# Revit family: Hager-UNIVERS-Hollow_wall-IP30-With_Cover-With_DIN-NoHosted-AT-de
name_source: partatom
category: Electrical Equipment
units: mm (PartAtom-declared; Revit-internal decimal feet)

## family parameters
Always vertical = Yes
Cut with Voids When Loaded = No
Maintain Annotation Orientation = No
Panel Configuration = Two Columns, Circuits Across
Part Type = Panelboard
Room Calculation Point = No
Round Connector Dimension = Use Diameter
Shared = No
Work Plane-Based = Yes

## types (21) — shared parameters
Code hager = ADD-EC000214_EU
Default Elevation = 1200 mm
EF000003 - Montageart = Hohlwand
EF000007 - Farbe = weiß
EF000024 - UV-beständig = No
EF000049 - Tiefe = 125 mm  [stored 0.410105 ft]
EF000116 - RAL-Nummer = 9010
EF000218 - Einbautiefe = 112 mm  [stored 0.367454 ft]
EF001062 - EMV-Ausführung = No
EF001088 - Anbaumöglichkeit = Yes
EF001134 - DIN-Schiene = Yes
EF004462 - Art der Schließung = sonstige
EF005474 - Schutzart (IP) = IP30
EF006244 - Transparenter Deckel/Tür = No
EF006306 - Mit Schloss = No
EF009212 - Ausführung Deckel = mit Ausschnitt
EF015776 - Erdungsklemmenblock = Yes
ETIM class code = EC000214
ETIM class name = Small distribution board
HG000002-Mit tür = Yes
HG000003-Bereich = UNIVERS
HG000005-Dicke = 2 mm  [stored 0.00656168 ft]
HG000006-Flush mounted = Yes
HG000012-Türschwenkwinkel = 90.00°
HG000013-Tür links = No
HG000014-Tür rechts = Yes
HG000015-Sichtbarkeit der Türöffnung = Yes
HG000016-3D-Türsichtbarkeit = Yes
HG000017-Distanz zwischen den Polen = 18 mm  [stored 0.0590551 ft]
HG000060-RAL-number = 9010
HG000099-Onfly Template ID-de-DE = 507532
Manufacturer = Hager
Name BIM&CO = Electricity
Name hager = ADD_Enclosures_EC000214
Reference = Template-Enclosure_EU-EC000214
Uniformat = Low Tension Service & Dist.
Uniformat code = D501001
zero-valued in all types: EF001131 - Innentiefe, HG000007-Anzahl der leeren Spalten

## per-type parameters (varying)
| type | BC_METADATA | EF000008 - Breite | EF000040 - Höhe | EF000118 - Mit Montageplatte | EF000266 - Anzahl der Reihen | EF000332 - Einbauhöhe | EF000846 - Einbaubreite | EF002950 - Breite in Teilungseinheiten | EF015777 - Neutralleiterklemmenblock | EF015941 - Signaldurchlassende Tür | HG000001-Anzahl der Spalten | HG000004-Herstellerreferenz | HG000008-Anzahl der leeren Reihen | HG000009-Doppelflügeligen Tür | HG000010-Asymmetrische Türen | HG000011-Leere Reihen von unten | HGEF000266-Anzahl der Reihen | HGEF0002950-Breite in Teilungseinheiten |
| UNIVERS-Hollow_wall_W603_H1153_D125_26_Modular_Spacing-FWU72M5 | {"ObjectGuid":"bf8f3bd7-583b-483a-8546-479ce88145ff","ModelGuid":"46e0040d-b32f-415f-bc34-bf38312fe43a","VariantGuid":"83216833-e940-4f8e-bb07-8edc410ff69f","Revision":"#6","VariantName":"UNIVERS-Hollow_wall_W603_H1153_D125_26_Modular_Spacing-FWU72M5"} | 603 mm | 1153 mm | No | 7 | 1102 mm  [stored 3.61549 ft] | 560 mm  [stored 1.83727 ft] | 26 | No | Yes | 1 | FWU72M5 | 4 | No | No | Yes | 7 | 26 |
| UNIVERS-Hollow_wall_W603_H1153_D125_24_Modular_Spacing-FWU72N2 | {"ObjectGuid":"bf8f3bd7-583b-483a-8546-479ce88145ff","ModelGuid":"46e0040d-b32f-415f-bc34-bf38312fe43a","VariantGuid":"d2052f01-a17f-49fd-b384-75a0194649ad","Revision":"#6","VariantName":"UNIVERS-Hollow_wall_W603_H1153_D125_24_Modular_Spacing-FWU72N2"} | 603 mm | 1153 mm | No | 7 | 1102 mm  [stored 3.61549 ft] | 560 mm  [stored 1.83727 ft] | 24 | No | No | 1 | FWU72N2 | 2 | No | No | No | 7 | 24 |
| UNIVERS-Hollow_wall_W603_H1153_D125_12_Modular_Spacing-FWU72S | {"ObjectGuid":"bf8f3bd7-583b-483a-8546-479ce88145ff","ModelGuid":"46e0040d-b32f-415f-bc34-bf38312fe43a","VariantGuid":"2965ec61-e6e9-4a88-9c4b-0654146b79c7","Revision":"#6","VariantName":"UNIVERS-Hollow_wall_W603_H1153_D125_12_Modular_Spacing-FWU72S"} | 603 mm | 1153 mm | No | 7 | 1102 mm  [stored 3.61549 ft] | 560 mm  [stored 1.83727 ft] | 12 | No | No | 2 | FWU72S | 0 | No | No | No | 7 | 12 |
| UNIVERS-Hollow_wall_W853_H1153_D125_12_Modular_Spacing-FWU73S | {"ObjectGuid":"bf8f3bd7-583b-483a-8546-479ce88145ff","ModelGuid":"46e0040d-b32f-415f-bc34-bf38312fe43a","VariantGuid":"00a44853-eb4c-43b7-9f09-506ca887cdd2","Revision":"#6","VariantName":"UNIVERS-Hollow_wall_W853_H1153_D125_12_Modular_Spacing-FWU73S"} | 853 mm  [stored 2.79856 ft] | 1153 mm | No | 7 | 1102 mm  [stored 3.61549 ft] | 810 mm | 12 | Yes | No | 3 | FWU73S | 0 | Yes | Yes | No | 7 | 12 |
| UNIVERS-Hollow_wall_W353_H553_D125_12_Modular_Spacing-FWU31S | {"ObjectGuid":"bf8f3bd7-583b-483a-8546-479ce88145ff","ModelGuid":"46e0040d-b32f-415f-bc34-bf38312fe43a","VariantGuid":"fd1da78a-eb51-489a-ae5e-f6d988f8db93","Revision":"#6","VariantName":"UNIVERS-Hollow_wall_W353_H553_D125_12_Modular_Spacing-FWU31S"} | 353 mm  [stored 1.15814 ft] | 553 mm  [stored 1.8143 ft] | No | 3 | 502 mm  [stored 1.64698 ft] | 310 mm  [stored 1.01706 ft] | 12 | Yes | No | 1 | FWU31S | 0 | No | No | No | 3 | 12 |
| UNIVERS-Hollow_wall_W603_H553_D125_12_Modular_Spacing-FWU32S | {"ObjectGuid":"bf8f3bd7-583b-483a-8546-479ce88145ff","ModelGuid":"46e0040d-b32f-415f-bc34-bf38312fe43a","VariantGuid":"bab0689f-0f9f-4e15-b462-dbcbb39ebcb3","Revision":"#6","VariantName":"UNIVERS-Hollow_wall_W603_H553_D125_12_Modular_Spacing-FWU32S"} | 603 mm | 553 mm  [stored 1.8143 ft] | No | 3 | 502 mm  [stored 1.64698 ft] | 560 mm  [stored 1.83727 ft] | 12 | No | No | 2 | FWU32S | 0 | No | No | No | 3 | 12 |
| UNIVERS-Hollow_wall_W853_H553_D125_12_Modular_Spacing-FWU33S | {"ObjectGuid":"bf8f3bd7-583b-483a-8546-479ce88145ff","ModelGuid":"46e0040d-b32f-415f-bc34-bf38312fe43a","VariantGuid":"66fc95c0-64b5-4e83-9b43-d419516fd529","Revision":"#6","VariantName":"UNIVERS-Hollow_wall_W853_H553_D125_12_Modular_Spacing-FWU33S"} | 853 mm  [stored 2.79856 ft] | 553 mm  [stored 1.8143 ft] | No | 3 | 502 mm  [stored 1.64698 ft] | 810 mm | 12 | No | No | 3 | FWU33S | 0 | Yes | Yes | No | 3 | 12 |
| UNIVERS-Hollow_wall_W353_H703_D125_12_Modular_Spacing-FWU41S | {"ObjectGuid":"bf8f3bd7-583b-483a-8546-479ce88145ff","ModelGuid":"46e0040d-b32f-415f-bc34-bf38312fe43a","VariantGuid":"75b65aa8-def3-42cf-aa5c-e2bfa099df58","Revision":"#6","VariantName":"UNIVERS-Hollow_wall_W353_H703_D125_12_Modular_Spacing-FWU41S"} | 353 mm  [stored 1.15814 ft] | 703 mm  [stored 2.30643 ft] | No | 4 | 652 mm  [stored 2.13911 ft] | 310 mm  [stored 1.01706 ft] | 12 | No | No | 1 | FWU41S | 0 | No | No | No | 4 | 12 |
| UNIVERS-Hollow_wall_W603_H703_D125_12_Modular_Spacing-FWU42S | {"ObjectGuid":"bf8f3bd7-583b-483a-8546-479ce88145ff","ModelGuid":"46e0040d-b32f-415f-bc34-bf38312fe43a","VariantGuid":"c91c35fe-13d6-4c48-a0a8-8c6b79d2b9b2","Revision":"#6","VariantName":"UNIVERS-Hollow_wall_W603_H703_D125_12_Modular_Spacing-FWU42S"} | 603 mm | 703 mm  [stored 2.30643 ft] | No | 4 | 652 mm  [stored 2.13911 ft] | 560 mm  [stored 1.83727 ft] | 12 | No | No | 2 | FWU42S | 0 | No | No | No | 4 | 12 |
| UNIVERS-Hollow_wall_W853_H703_D125_12_Modular_Spacing-FWU43S | {"ObjectGuid":"bf8f3bd7-583b-483a-8546-479ce88145ff","ModelGuid":"46e0040d-b32f-415f-bc34-bf38312fe43a","VariantGuid":"49b9ddb8-8c9f-4eb5-bc56-9bb4d504d377","Revision":"#6","VariantName":"UNIVERS-Hollow_wall_W853_H703_D125_12_Modular_Spacing-FWU43S"} | 853 mm  [stored 2.79856 ft] | 703 mm  [stored 2.30643 ft] | No | 4 | 652 mm  [stored 2.13911 ft] | 810 mm | 12 | No | No | 3 | FWU43S | 0 | Yes | Yes | No | 4 | 12 |
| UNIVERS-Hollow_wall_W353_H853_D125_12_Modular_Spacing-FWU51S | {"ObjectGuid":"bf8f3bd7-583b-483a-8546-479ce88145ff","ModelGuid":"46e0040d-b32f-415f-bc34-bf38312fe43a","VariantGuid":"a0978855-299b-4b4f-81af-e42c7cc2ba0c","Revision":"#6","VariantName":"UNIVERS-Hollow_wall_W353_H853_D125_12_Modular_Spacing-FWU51S"} | 353 mm  [stored 1.15814 ft] | 853 mm  [stored 2.79856 ft] | No | 5 | 802 mm  [stored 2.63123 ft] | 310 mm  [stored 1.01706 ft] | 12 | No | No | 1 | FWU51S | 0 | No | No | No | 5 | 12 |
| UNIVERS-Hollow_wall_W603_H853_D125_26_Modular_Spacing-FWU52M5 | {"ObjectGuid":"bf8f3bd7-583b-483a-8546-479ce88145ff","ModelGuid":"46e0040d-b32f-415f-bc34-bf38312fe43a","VariantGuid":"4c46465e-c1f1-4e1c-a3aa-39c010eefd45","Revision":"#6","VariantName":"UNIVERS-Hollow_wall_W603_H853_D125_26_Modular_Spacing-FWU52M5"} | 603 mm | 853 mm  [stored 2.79856 ft] | Yes | 5 | 802 mm  [stored 2.63123 ft] | 560 mm  [stored 1.83727 ft] | 26 | No | Yes | 1 | FWU52M5 | 2 | No | No | Yes | 5 | 26 |
| UNIVERS-Hollow_wall_W603_H853_D125_24_Modular_Spacing-FWU52N2 | {"ObjectGuid":"bf8f3bd7-583b-483a-8546-479ce88145ff","ModelGuid":"46e0040d-b32f-415f-bc34-bf38312fe43a","VariantGuid":"f8ee8a13-e1e7-47bc-9432-14c594f627e9","Revision":"#6","VariantName":"UNIVERS-Hollow_wall_W603_H853_D125_24_Modular_Spacing-FWU52N2"} | 603 mm | 853 mm  [stored 2.79856 ft] | No | 5 | 802 mm  [stored 2.63123 ft] | 560 mm  [stored 1.83727 ft] | 24 | No | No | 1 | FWU52N2 | 2 | No | No | No | 5 | 24 |
| UNIVERS-Hollow_wall_W603_H853_D125_12_Modular_Spacing-FWU52S | {"ObjectGuid":"bf8f3bd7-583b-483a-8546-479ce88145ff","ModelGuid":"46e0040d-b32f-415f-bc34-bf38312fe43a","VariantGuid":"7fb96306-1119-4e5f-bdf7-75aa8be4df15","Revision":"#6","VariantName":"UNIVERS-Hollow_wall_W603_H853_D125_12_Modular_Spacing-FWU52S"} | 603 mm | 853 mm  [stored 2.79856 ft] | No | 5 | 802 mm  [stored 2.63123 ft] | 560 mm  [stored 1.83727 ft] | 12 | No | No | 2 | FWU52S | 0 | No | No | No | 5 | 12 |
| UNIVERS-Hollow_wall_W353_H1003_D125_12_Modular_Spacing-FWU61M5 | {"ObjectGuid":"bf8f3bd7-583b-483a-8546-479ce88145ff","ModelGuid":"46e0040d-b32f-415f-bc34-bf38312fe43a","VariantGuid":"a9de7a1b-e03c-4555-82ff-78d63b21a8da","Revision":"#6","VariantName":"UNIVERS-Hollow_wall_W353_H1003_D125_12_Modular_Spacing-FWU61M5"} | 353 mm  [stored 1.15814 ft] | 1003 mm  [stored 3.29068 ft] | Yes | 6 | 952 mm  [stored 3.12336 ft] | 310 mm  [stored 1.01706 ft] | 12 | No | Yes | 1 | FWU61M5 | 3 | No | No | Yes | 6 | 12 |
| UNIVERS-Hollow_wall_W353_H1003_D125_12_Modular_Spacing-FWU61S | {"ObjectGuid":"bf8f3bd7-583b-483a-8546-479ce88145ff","ModelGuid":"46e0040d-b32f-415f-bc34-bf38312fe43a","VariantGuid":"64352249-4482-4bb7-bf02-fa5fb5e34fb1","Revision":"#6","VariantName":"UNIVERS-Hollow_wall_W353_H1003_D125_12_Modular_Spacing-FWU61S"} | 353 mm  [stored 1.15814 ft] | 1003 mm  [stored 3.29068 ft] | No | 6 | 952 mm  [stored 3.12336 ft] | 310 mm  [stored 1.01706 ft] | 12 | No | No | 1 | FWU61S | 0 | No | No | No | 6 | 12 |
| UNIVERS-Hollow_wall_W603_H1003_D125_26_Modular_Spacing-FWU62M5 | {"ObjectGuid":"bf8f3bd7-583b-483a-8546-479ce88145ff","ModelGuid":"46e0040d-b32f-415f-bc34-bf38312fe43a","VariantGuid":"0d453e49-a1aa-4379-8210-e4f66013d88a","Revision":"#6","VariantName":"UNIVERS-Hollow_wall_W603_H1003_D125_26_Modular_Spacing-FWU62M5"} | 603 mm | 1003 mm  [stored 3.29068 ft] | Yes | 6 | 952 mm  [stored 3.12336 ft] | 560 mm  [stored 1.83727 ft] | 26 | No | Yes | 1 | FWU62M5 | 3 | No | No | Yes | 6 | 26 |
| UNIVERS-Hollow_wall_W603_H1003_D125_24_Modular_Spacing-FWU62N2 | {"ObjectGuid":"bf8f3bd7-583b-483a-8546-479ce88145ff","ModelGuid":"46e0040d-b32f-415f-bc34-bf38312fe43a","VariantGuid":"f768c7a1-f6c7-413e-a407-54643779568c","Revision":"#6","VariantName":"UNIVERS-Hollow_wall_W603_H1003_D125_24_Modular_Spacing-FWU62N2"} | 603 mm | 1003 mm  [stored 3.29068 ft] | No | 6 | 952 mm  [stored 3.12336 ft] | 560 mm  [stored 1.83727 ft] | 24 | No | No | 1 | FWU62N2 | 2 | No | No | No | 6 | 24 |
| UNIVERS-Hollow_wall_W603_H1003_D125_12_Modular_Spacing-FWU62S | {"ObjectGuid":"bf8f3bd7-583b-483a-8546-479ce88145ff","ModelGuid":"46e0040d-b32f-415f-bc34-bf38312fe43a","VariantGuid":"c31bbf05-6cf6-473e-a596-203c1bf58c29","Revision":"#6","VariantName":"UNIVERS-Hollow_wall_W603_H1003_D125_12_Modular_Spacing-FWU62S"} | 603 mm | 1003 mm  [stored 3.29068 ft] | No | 6 | 952 mm  [stored 3.12336 ft] | 560 mm  [stored 1.83727 ft] | 12 | No | No | 2 | FWU62S | 0 | No | No | No | 6 | 12 |
| UNIVERS-Hollow_wall_W853_H1003_D125_12_Modular_Spacing-FWU63S | {"ObjectGuid":"bf8f3bd7-583b-483a-8546-479ce88145ff","ModelGuid":"46e0040d-b32f-415f-bc34-bf38312fe43a","VariantGuid":"c59c75c7-18a2-4a6b-8e2d-f12753ba91d4","Revision":"#6","VariantName":"UNIVERS-Hollow_wall_W853_H1003_D125_12_Modular_Spacing-FWU63S"} | 853 mm  [stored 2.79856 ft] | 1003 mm  [stored 3.29068 ft] | No | 6 | 952 mm  [stored 3.12336 ft] | 810 mm | 12 | No | No | 3 | FWU63S | 0 | Yes | Yes | No | 6 | 12 |
| UNIVERS-Hollow_wall_W353_H1153_D125_12_Modular_Spacing-FWU71S | {"ObjectGuid":"bf8f3bd7-583b-483a-8546-479ce88145ff","ModelGuid":"46e0040d-b32f-415f-bc34-bf38312fe43a","VariantGuid":"230cc608-0a26-46fe-b395-6b6693e030f5","Revision":"#6","VariantName":"UNIVERS-Hollow_wall_W353_H1153_D125_12_Modular_Spacing-FWU71S"} | 353 mm  [stored 1.15814 ft] | 1153 mm | No | 7 | 1102 mm  [stored 3.61549 ft] | 310 mm  [stored 1.01706 ft] | 12 | No | No | 1 | FWU71S | 0 | No | No | No | 7 | 12 |

note: [stored X ft] marks values corroborated as IEEE doubles in the binary element streams (Revit-internal decimal feet)

## geometry (parser evidence)
native form markers: Sweep x15
no freeform markers — native parametric forms only
